# Revit family: BIMON_Котел_Водогрейный_TEMRON_WL3000
name_source: partatom
category: Оборудование
units: mm (PartAtom-declared; Revit-internal decimal feet)

## family parameters
Всегда вертикально = Да
Классификация = Нет
На основе рабочей плоскости = Нет
Общий = Нет
При загрузке вырезать с полостями = Нет
Размер круглого соединителя = Использовать диаметр
Тип детали = Нормальный
Точка расчета площади = Нет

## types (1)
- BIMON_Котел_Водогрейный_TEMRON_WL3000
    ADSK_URL страницы изделия = https://temron.ru
    ADSK_Единица измерения = шт
    ADSK_Завод-изготовитель = Temron
    ADSK_Количество = 1
    ADSK_Марка = WL 3000
    ADSK_Масса = 4466
    ADSK_Масса_Текст = 4466
    ADSK_Материал = <По категории>
    ADSK_Наименование = Водогрейный котел низкого давления
    ADSK_Обозначение = WL 3000
    D1_Вход теплоносителя = 200 мм
    D1_Выход теплоносителя = 200 мм
    D2_Аварийная линия = 50 мм
    D3_Дренажный патрубок = 32 мм
    D4_Дренажный патрубок газового котла = 15 мм
    D5_Уходящие газы = 590 мм
    TEMRON_Водяной объём котла = 3.6 м³
    TEMRON_КПД = 92.4 %
    TEMRON_Максимальная температура пара = 110 мм
    TEMRON_Максимальное рабочее давление = 0.6 МПа
    TEMRON_Номинальная производительность = 3 МВт
    TEMRON_Расход воды через котел = 103.1 м³/ч
    TEMRON_Расход топлива для природного газа = 328.3 м³/ч
    TEMRON_Сопротивление газового тракта = 8 мбар
    TEMRON_Температура на входе в котёл = 60 °С
    TEMRON_Температура на выходе из котла = 110 °С
    TEMRON_Температура уходящих газов = 180-185 /185-190 °С
    TEMRON_Теплопроизводительность = 3 МВт/2.579 (Гкал/ч)
    TERMON_Расход уходящих газов = 4892 кг/ч
    URL = https://temron.ru
    Изготовитель = Temron
    Разработчик = BIMON
    Разработчик_Сайт = https://www.bimon.ru
